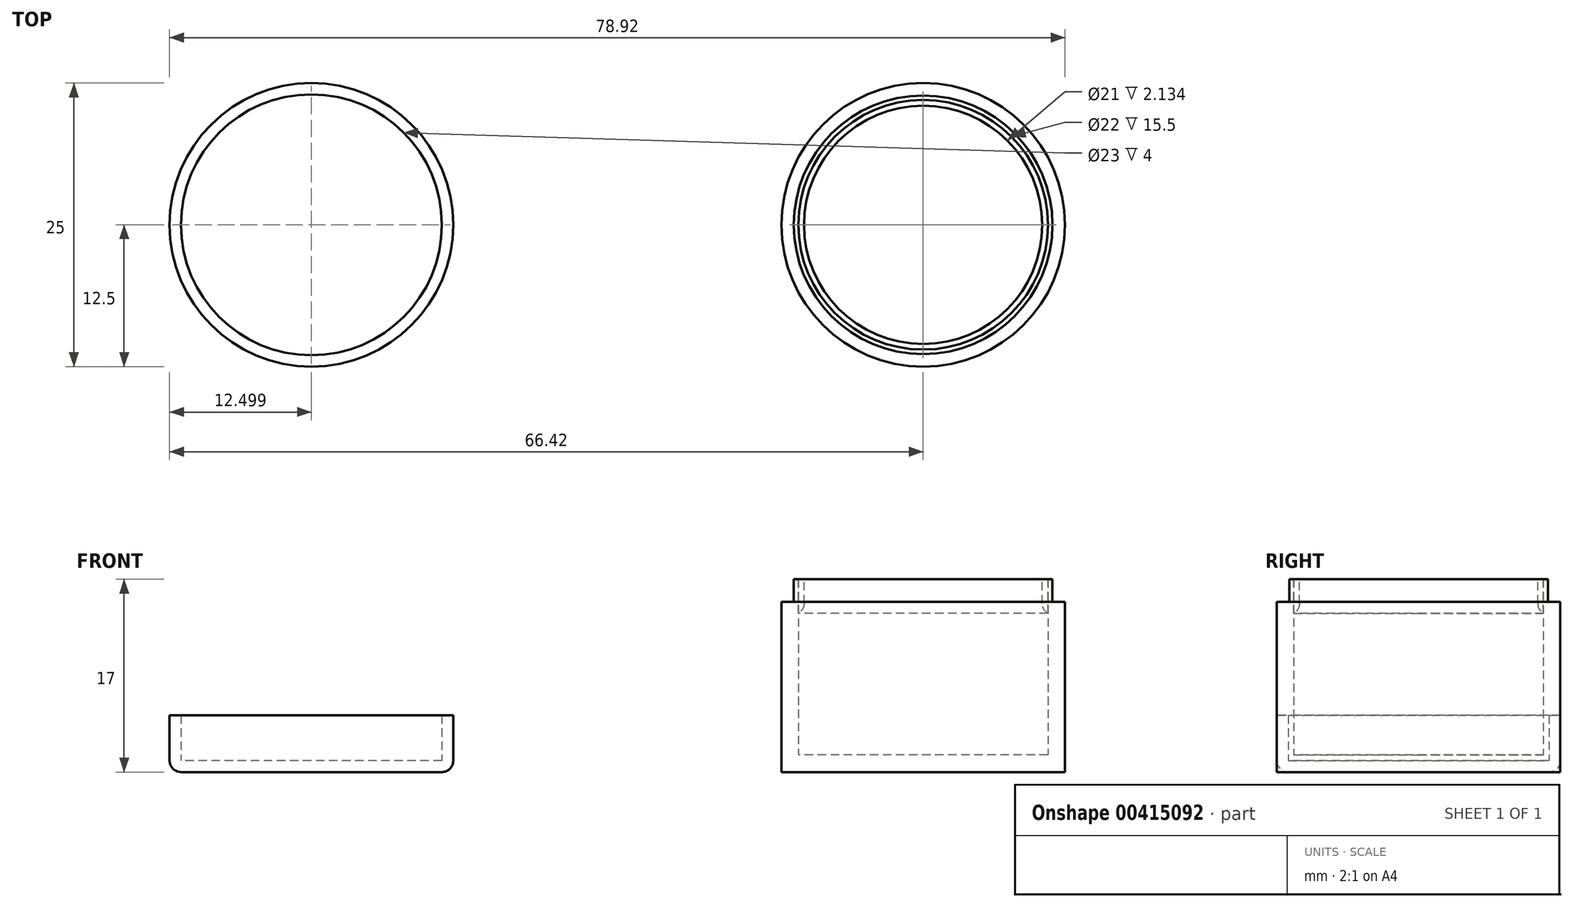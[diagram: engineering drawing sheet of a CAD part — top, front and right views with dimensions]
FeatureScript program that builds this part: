
annotation { "Feature Type Name" : "Feature", "Feature Type Description" : "" }
export const myFeature = defineFeature(function(context is Context, id is Id, definition is map)
    precondition{}
    {
        {
            var Q0;
            Q0=qCreatedBy(makeId("Top.planeOp"),FACE);
            var sketch = newSketch(context, id + "F0", { "sketchPlane" : qUnion([Q0])});
            skCircle(sketch, "E0", {"center": v(0, 0) * mm, "radius": 12.5 * mm});
            skSolve(sketch);
        }
        {
            var Q0;
            Q0=makeQuery(id+"F0.imprint","IMPRINT",FACE,{"disambiguationData":[TD([[makeQuery(id+"F0.imprint","IMPRINT",EDGE,{"derivedFrom":sQuery(id+"F0.wireOp",EDGE,"E0")}),1.0]])]});
            extrude(context, id + "F1", {"entities" : qUnion([Q0]), "depth" : 15 * mm});
        }
        {
            var Q0;
            Q0=makeQuery(id+"F1.opExtrude","CAP_FACE",FACE,{"disambiguationData":[OSD([sQuery(id+"F0.wireOp",EDGE,"E0")])],"isStart":false});
            shell(context, id + "F2", {"entities" : qUnion([Q0]), "thickness" : 1.5 * mm});
        }
        {
            var Q0;
            Q0=makeQuery(id+"F1.opExtrude","CAP_FACE",FACE,{"disambiguationData":[OSD([sQuery(id+"F0.wireOp",EDGE,"E0")])],"isStart":false});
            var sketch = newSketch(context, id + "F3", { "sketchPlane" : qUnion([Q0])});
            skCircle(sketch, "E1", {"center": v(0, 0) * mm, "radius": 11 * mm});
            skCircle(sketch, "E2", {"center": v(0, 0) * mm, "radius": 11.4 * mm});
            skSolve(sketch);
        }
        {
            var Q0;
            Q0 = qSketchRegion(id + "F3", true);
            extrude(context, id + "F4", {"entities" : qUnion([Q0]), "operationType" : NewBodyOperationType.ADD, "depth" : 2 * mm});
        }
        {
            var Q0;
            Q0=qCreatedBy(makeId("Top.planeOp"),FACE);
            var sketch = newSketch(context, id + "F5", { "sketchPlane" : qUnion([Q0])});
            skCircle(sketch, "E3", {"center": v(-53.92, 0) * mm, "radius": 12.5 * mm});
            skSolve(sketch);
        }
        {
            var Q0;
            Q0=makeQuery(id+"F5.imprint","IMPRINT",FACE,{"disambiguationData":[TD([[makeQuery(id+"F5.imprint","IMPRINT",EDGE,{"derivedFrom":sQuery(id+"F5.wireOp",EDGE,"E3")}),1.0]])]});
            extrude(context, id + "F6", {"entities" : qUnion([Q0]), "depth" : 5 * mm});
        }
        {
            var Q0;
            Q0=makeQuery(id+"F6.opExtrude","CAP_FACE",FACE,{"disambiguationData":[OSD([sQuery(id+"F5.wireOp",EDGE,"E3")])],"isStart":false});
            shell(context, id + "F7", {"entities" : qUnion([Q0]), "thickness" : 1 * mm});
        }
        {
            var Q0;
            Q0=makeQuery(id+"F6.opExtrude","CAP_FACE",FACE,{"disambiguationData":[OSD([sQuery(id+"F5.wireOp",EDGE,"E3")])],"isStart":true});
            fillet(context, id + "F8", {"entities" : qUnion([Q0]), "radius" : 1 * mm, "tangentPropagation" : true, "allowEdgeOverflow" : false});
        }
        {
            var Q0;
            {var subQ0=sQuery(id+"F5.wireOp",EDGE,"E3");Q0=makeQuery(id+"F7.opShell","OFFSET_FACE",FACE,{"disambiguationData":[OSD([subQ0]),TDD([makeQuery(id+"F6.opExtrude","CAP_FACE",FACE,{"disambiguationData":[OSD([subQ0])],"isStart":true})])]});}
            var sketch = newSketch(context, id + "F9", { "sketchPlane" : qUnion([Q0])});
            skCircle(sketch, "E4", {"center": v(-53.92, 0) * mm, "radius": 7.16 * mm, "construction": true});
            skCircle(sketch, "E5", {"center": v(-53.92, 7.16) * mm, "radius": 1.5 * mm});
            skSolve(sketch);
        }
        {
            var Q0;
            Q0=makeQuery(id+"F4.opExtrude","CAP_FACE",FACE,{"disambiguationData":[OSD([sQuery(id+"F3.wireOp",EDGE,"E1"),sQuery(id+"F3.wireOp",EDGE,"E2")])],"isStart":false});
            var sketch = newSketch(context, id + "F10", { "sketchPlane" : qUnion([Q0])});
            skCircle(sketch, "E6", {"center": v(0, 0) * mm, "radius": 11 * mm});
            skCircle(sketch, "E7", {"center": v(0, 0) * mm, "radius": 10.5 * mm});
            skSolve(sketch);
        }
        {
            var Q0;
            Q0=makeQuery(id+"F10.imprint","IMPRINT",FACE,{"disambiguationData":[TD([[makeQuery(id+"F10.imprint","IMPRINT",EDGE,{"derivedFrom":sQuery(id+"F10.wireOp",EDGE,"E6")}),1.0]])]});
            extrude(context, id + "F11", {"entities" : qUnion([Q0]), "oppositeDirection" : true, "depth" : 3 * mm, "offsetDistance" : 25 * mm});
        }
        {
            var Q0;
            Q0=makeQuery(id+"F11.opExtrude","CAP_EDGE",EDGE,{"disambiguationData":[OSD([sQuery(id+"F10.wireOp",EDGE,"E7")])],"isStart":false});
            fillet(context, id + "F12", {"entities" : qUnion([Q0]), "tangentPropagation" : true, "radius" : 1 * mm, "defaultsChanged" : false, "vertexSettings" : [], "allowEdgeOverflow" : false});
        }
    });
